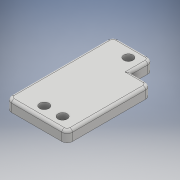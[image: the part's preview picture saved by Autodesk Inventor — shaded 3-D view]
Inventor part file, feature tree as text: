
AUTODESK INVENTOR PART (.ipt)
format: ipt  version: 2018 (Build 220112000, 112)  size: 166,912 bytes
history: native  units: mm
features: other x4, reference x3, extrude x2, fillet x2, sketch x2, plane x1
ambient origin geometry x8: Origin, YZ Plane, XZ Plane, XY Plane, X Axis, Y Axis, Z Axis, Center Point
bodies: Body1 (feature_tree)
feature tree (14):
  plane  "Work Plane1"
  extrude  "Extrusion3"  Depth=4.0mm
  extrude  "Extrusion4"  Depth=1.0mm
  fillet  "Fillet1"  Radius=6.0mm
  fillet  "Fillet2"  Radius=3.5mm
  sketch  "Sketch5"  dims[d12=4.0mm d13=0.0mm d14=5.0mm]
  reference  "Reference8"
  reference  "Reference9"
  reference  "Reference10"
  sketch  "Sketch6"  dims[d15=3.5mm d16=4.285mm d17=6.0mm d18=3.5mm d19=10.0mm d20=3.5mm d21=4.0mm d22=0.0mm d23=2.0mm d24=1.0mm]
  other  "<userpath>\OneDrive\Documents\Inventor\TSA\2018\Animatronics\Tortoise\Turtle3.iam"
  other  "Turtle3.iam"
  other  "SyringeMotorBase:1"
  other  "servo (2)_MIR:3"
